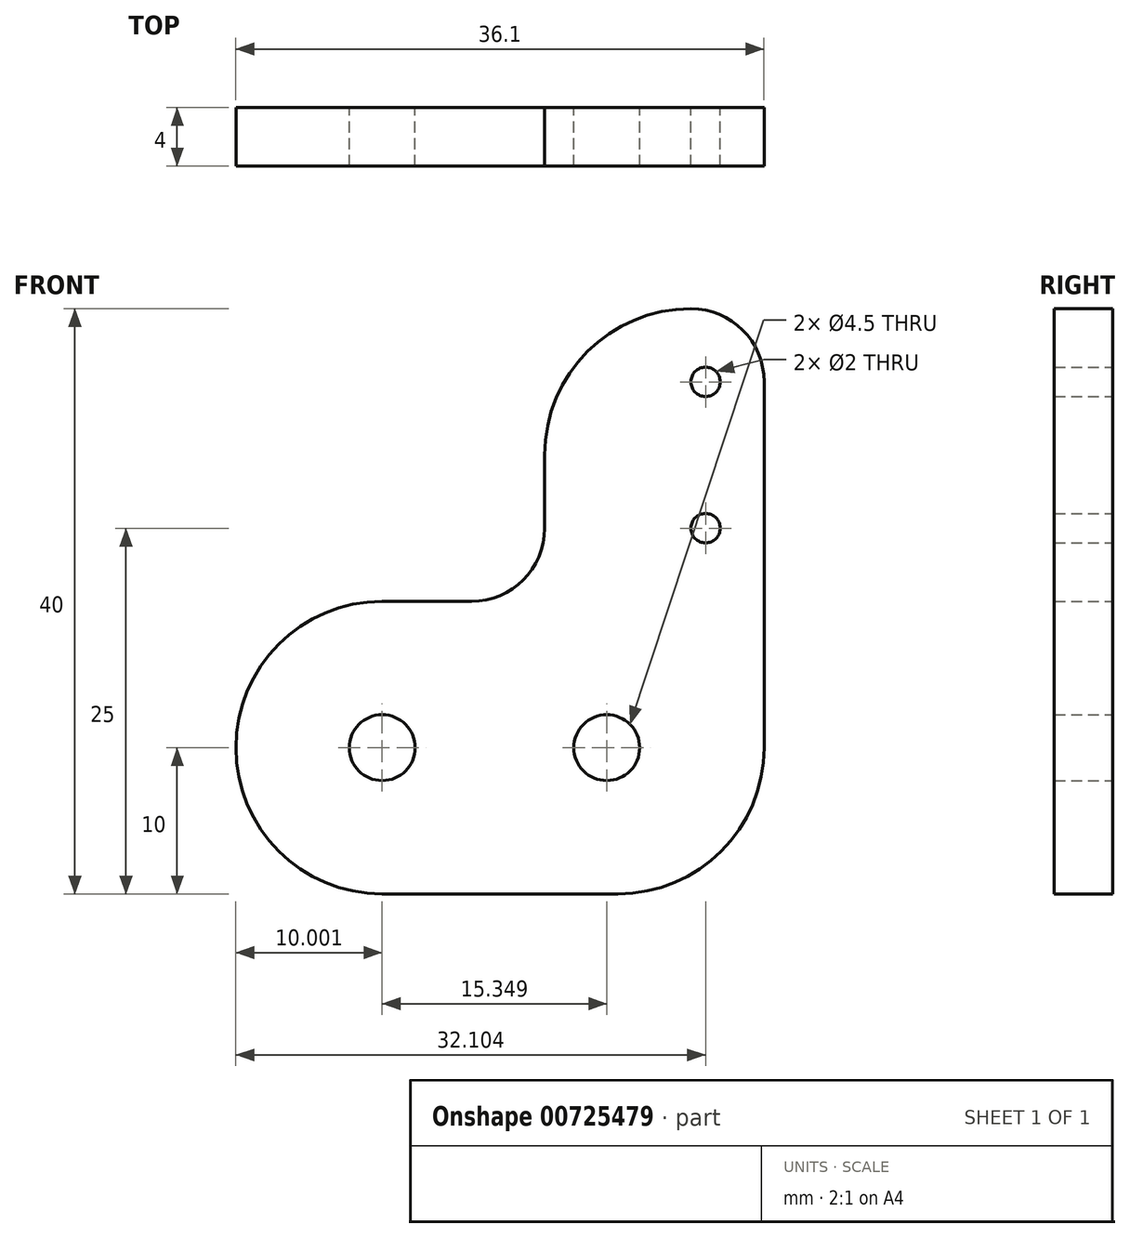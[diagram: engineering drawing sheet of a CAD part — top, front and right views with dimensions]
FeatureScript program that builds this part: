
annotation { "Feature Type Name" : "Feature", "Feature Type Description" : "" }
export const myFeature = defineFeature(function(context is Context, id is Id, definition is map)
    precondition{}
    {
        {
            var Q0;
            Q0=qCreatedBy(makeId("Front.planeOp"),FACE);
            var sketch = newSketch(context, id + "F0", { "sketchPlane" : qUnion([Q0])});
            skCircle(sketch, "E0", {"center": v(0, 0) * mm, "radius": 2.25 * mm});
            skCircle(sketch, "E1", {"center": v(-15.35, 0) * mm, "radius": 2.25 * mm});
            skArc(sketch, "E2", {"start": v(-15.35, 10) * mm, "mid": v(-25.35, 0) * mm, "end": v(-15.35, -10) * mm});
            skLineSegment(sketch, "E3", {"start": v(-15.35, -10) * mm, "end": v(0, -10) * mm});
            skLineSegment(sketch, "E4", {"start": v(-15.35, 10) * mm, "end": v(-9.25, 10) * mm});
            skLineSegment(sketch, "E5", {"start": v(0.75, 0) * mm, "end": v(10.75, 0) * mm});
            skLineSegment(sketch, "E6", {"start": v(10.75, 0) * mm, "end": v(10.75, 10) * mm});
            skLineSegment(sketch, "E7", {"start": v(10.75, 10) * mm, "end": v(10.75, 15) * mm});
            skLineSegment(sketch, "E8", {"start": v(10.75, 15) * mm, "end": v(10.75, 25) * mm});
            skLineSegment(sketch, "E9", {"start": v(10.75, 25) * mm, "end": v(10.75, 25) * mm});
            skLineSegment(sketch, "E10", {"start": v(5.75, 30) * mm, "end": v(5.75, 30) * mm});
            skLineSegment(sketch, "E11", {"start": v(-4.25, 20) * mm, "end": v(-4.25, 15) * mm});
            skLineSegment(sketch, "E12", {"start": v(0, -10) * mm, "end": v(0.75, -10) * mm});
            skLineSegment(sketch, "E13", {"start": v(10.75, 0) * mm, "end": v(10.75, 0) * mm});
            skPoint(sketch, "E14.visualSharp", {"position": v(-4.25, 30) * mm});
            skArc(sketch, "E14.filletArc", {"start": v(5.75, 30) * mm, "mid": v(-1.32, 27.07) * mm, "end": v(-4.25, 20) * mm});
            skPoint(sketch, "E15.visualSharp", {"position": v(10.75, -10) * mm});
            skArc(sketch, "E15.filletArc", {"start": v(0.75, -10) * mm, "mid": v(7.83, -7.07) * mm, "end": v(10.75, 0) * mm});
            skPoint(sketch, "E16.newPointB", {"position": v(0, 10) * mm});
            skArc(sketch, "E16.filletArc", {"start": v(-9.25, 10) * mm, "mid": v(-5.71, 11.46) * mm, "end": v(-4.25, 15) * mm});
            skPoint(sketch, "E17.visualSharp", {"position": v(10.75, 30) * mm});
            skArc(sketch, "E17.filletArc", {"start": v(10.75, 25) * mm, "mid": v(9.29, 28.54) * mm, "end": v(5.75, 30) * mm});
            skCircle(sketch, "E18", {"center": v(6.75, 15) * mm, "radius": 1 * mm});
            skCircle(sketch, "E19", {"center": v(6.75, 25) * mm, "radius": 1 * mm});
            skSolve(sketch);
        }
        {
            var Q0;
            Q0=makeQuery(id+"F0.imprint","IMPRINT",FACE,{"disambiguationData":[TD([[makeQuery(id+"F0.imprint","IMPRINT",EDGE,{"derivedFrom":sQuery(id+"F0.wireOp",EDGE,"E0")}),-1.0]])]});
            extrude(context, id + "F1", {"entities" : qUnion([Q0]), "depth" : 4 * mm, "offsetDistance" : 25 * mm});
        }
    });
